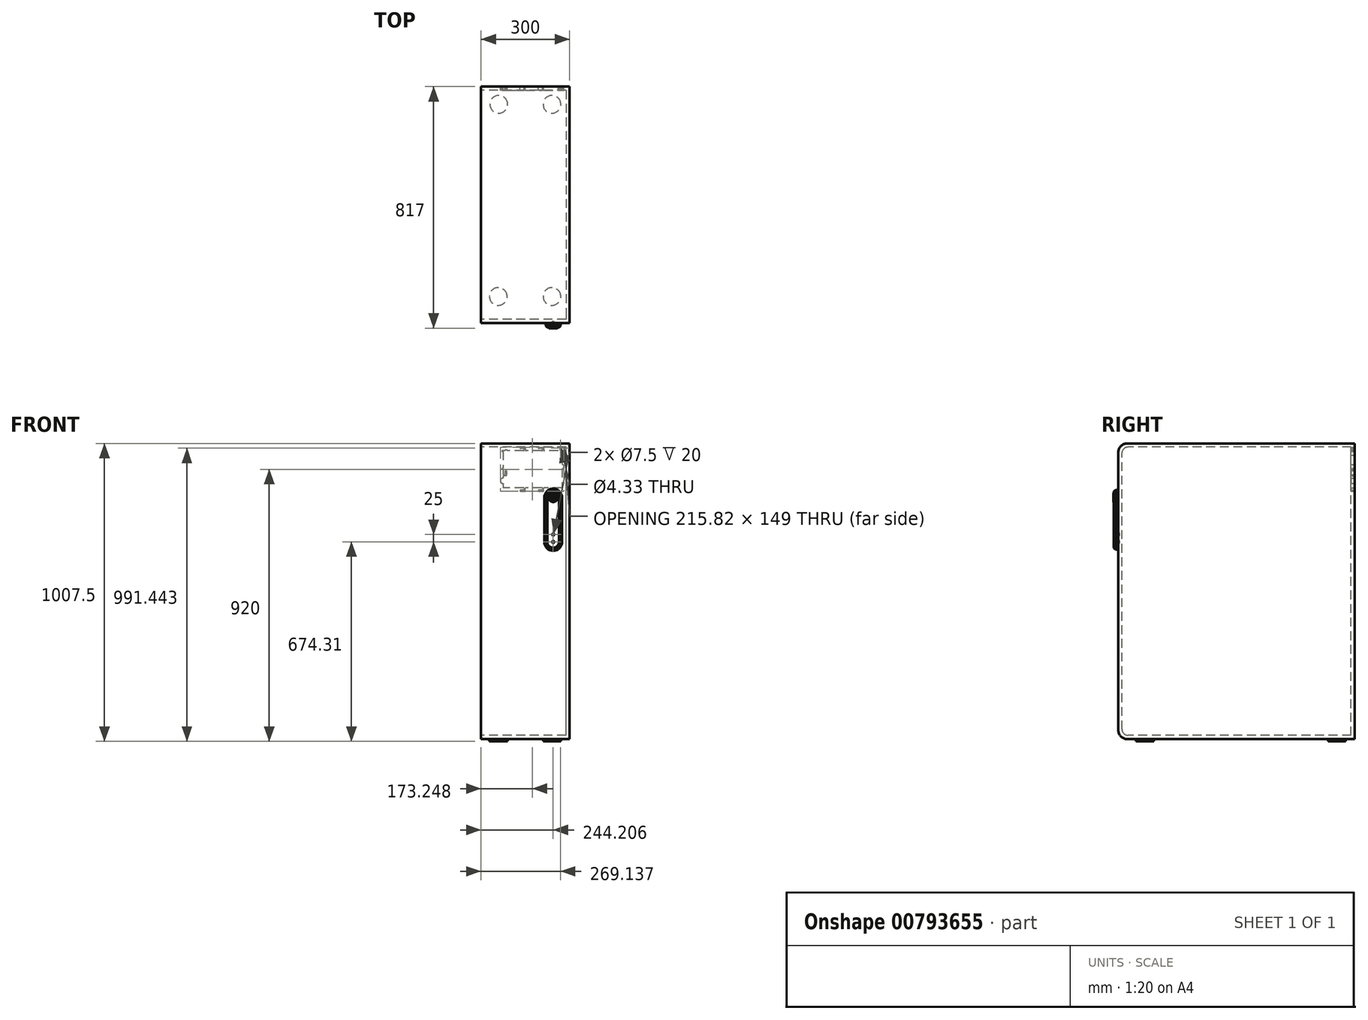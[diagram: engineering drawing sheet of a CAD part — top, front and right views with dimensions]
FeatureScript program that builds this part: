
annotation { "Feature Type Name" : "Feature", "Feature Type Description" : "" }
export const myFeature = defineFeature(function(context is Context, id is Id, definition is map)
    precondition{}
    {
        {
            var Q0;
            Q0=qCreatedBy(makeId("Right.planeOp"),FACE);
            var sketch = newSketch(context, id + "F0", { "sketchPlane" : qUnion([Q0])});
            skLineSegment(sketch, "E0.bottom", {"start": v(400, -500) * mm, "end": v(-400, -500) * mm});
            skLineSegment(sketch, "E0.top", {"start": v(400, 500) * mm, "end": v(-400, 500) * mm});
            skLineSegment(sketch, "E0.left", {"start": v(400, -500) * mm, "end": v(400, 500) * mm});
            skLineSegment(sketch, "E0.right", {"start": v(-400, -500) * mm, "end": v(-400, 500) * mm});
            skPoint(sketch, "E0.middle", {"position": v(0, 0) * mm});
            skSolve(sketch);
        }
        {
            var Q0;
            Q0=makeQuery(id+"F0.imprint","IMPRINT",FACE,{"disambiguationData":[TD([[makeQuery(id+"F0.imprint","IMPRINT",EDGE,{"derivedFrom":sQuery(id+"F0.wireOp",EDGE,"E0.bottom")}),-1.0]])]});
            extrude(context, id + "F1", {"entities" : qUnion([Q0]), "depth" : 300 * mm, "offsetDistance" : 25 * mm});
        }
        {
            var Q0;
            Q0=makeQuery(id+"F1.opExtrude","SWEPT_EDGE",EDGE,{"disambiguationData":[OSD([sQuery(id+"F0.wireOp",EDGE,"E0.top"),sQuery(id+"F0.wireOp",EDGE,"E0.right")])]});
            var Q1;
            Q1=makeQuery(id+"F1.opExtrude","SWEPT_EDGE",EDGE,{"disambiguationData":[OSD([sQuery(id+"F0.wireOp",EDGE,"E0.bottom"),sQuery(id+"F0.wireOp",EDGE,"E0.right")])]});
            fillet(context, id + "F2", {"entities" : qUnion([Q0, Q1]), "radius" : 30 * mm, "tangentPropagation" : true, "allowEdgeOverflow" : false});
        }
        {
            var Q0;
            Q0=makeQuery(id+"F1.opExtrude","CAP_FACE",FACE,{"disambiguationData":[OSD([sQuery(id+"F0.wireOp",EDGE,"E0.bottom"),sQuery(id+"F0.wireOp",EDGE,"E0.top"),sQuery(id+"F0.wireOp",EDGE,"E0.left"),sQuery(id+"F0.wireOp",EDGE,"E0.right")])],"isStart":true});
            var sketch = newSketch(context, id + "F3", { "sketchPlane" : qUnion([Q0])});
            skLineSegment(sketch, "E1.bottom", {"start": v(-387.5, -487.5) * mm, "end": v(367.5, -487.5) * mm});
            skLineSegment(sketch, "E1.top", {"start": v(-387.5, 487.5) * mm, "end": v(367.5, 487.5) * mm});
            skLineSegment(sketch, "E1.left", {"start": v(-387.5, -487.5) * mm, "end": v(-387.5, 487.5) * mm});
            skLineSegment(sketch, "E1.right", {"start": v(387.5, -467.5) * mm, "end": v(387.5, 467.5) * mm});
            skPoint(sketch, "E1.middle", {"position": v(0, 0) * mm});
            skPoint(sketch, "E2.visualSharp", {"position": v(387.5, 487.5) * mm});
            skArc(sketch, "E2.filletArc", {"start": v(387.5, 467.5) * mm, "mid": v(381.64, 481.64) * mm, "end": v(367.5, 487.5) * mm});
            skPoint(sketch, "E3.visualSharp", {"position": v(387.5, -487.5) * mm});
            skArc(sketch, "E3.filletArc", {"start": v(367.5, -487.5) * mm, "mid": v(381.64, -481.64) * mm, "end": v(387.5, -467.5) * mm});
            skSolve(sketch);
        }
        {
            var Q0;
            Q0=makeQuery(id+"F3.imprint","IMPRINT",FACE,{"disambiguationData":[TD([[makeQuery(id+"F3.imprint","IMPRINT",EDGE,{"derivedFrom":sQuery(id+"F3.wireOp",EDGE,"E1.bottom")}),1.0]])]});
            extrude(context, id + "F4", {"entities" : qUnion([Q0]), "operationType" : NewBodyOperationType.REMOVE, "oppositeDirection" : true, "depth" : 287.5 * mm, "offsetDistance" : 25 * mm});
        }
        {
            var Q0;
            Q0=makeQuery(id+"F1.opExtrude","SWEPT_FACE",FACE,{"disambiguationData":[OSD([sQuery(id+"F0.wireOp",EDGE,"E0.left")])]});
            var sketch = newSketch(context, id + "F5", { "sketchPlane" : qUnion([Q0])});
            skLineSegment(sketch, "E4.bottom", {"start": v(-261.46, 475) * mm, "end": v(-214.12, 475) * mm});
            skLineSegment(sketch, "E4.top", {"start": v(-274.34, 350) * mm, "end": v(-214.12, 350) * mm});
            skLineSegment(sketch, "E4.left", {"start": v(-274.34, 459.64) * mm, "end": v(-274.34, 428.5) * mm});
            skLineSegment(sketch, "E4.right", {"start": v(-74.34, 473) * mm, "end": v(-74.34, 415.52) * mm});
            skLineSegment(sketch, "E5", {"start": v(-74.34, 475) * mm, "end": v(-71.34, 475) * mm});
            skLineSegment(sketch, "E6", {"start": v(-70.34, 474) * mm, "end": v(-70.34, 474) * mm});
            skLineSegment(sketch, "E7", {"start": v(-71.34, 473) * mm, "end": v(-74.34, 473) * mm});
            skPoint(sketch, "E8.visualSharp", {"position": v(-70.34, 473) * mm});
            skArc(sketch, "E8.filletArc", {"start": v(-71.34, 473) * mm, "mid": v(-70.63, 473.3) * mm, "end": v(-70.34, 474) * mm});
            skPoint(sketch, "E9.visualSharp", {"position": v(-70.34, 475) * mm});
            skArc(sketch, "E9.filletArc", {"start": v(-70.34, 474) * mm, "mid": v(-70.63, 474.7) * mm, "end": v(-71.34, 475) * mm});
            skArc(sketch, "E10", {"start": v(-81.43, 475) * mm, "mid": v(-84.93, 478.5) * mm, "end": v(-88.43, 475) * mm});
            skLineSegment(sketch, "E11.trimOffspring", {"start": v(-81.43, 475) * mm, "end": v(-74.34, 475) * mm});
            skLineSegment(sketch, "E12", {"start": v(-146.17, 477) * mm, "end": v(-146.17, 481) * mm});
            skLineSegment(sketch, "E13", {"start": v(-144.17, 483) * mm, "end": v(-134.17, 483) * mm});
            skLineSegment(sketch, "E14", {"start": v(-134.17, 487) * mm, "end": v(-148.17, 487) * mm});
            skLineSegment(sketch, "E15", {"start": v(-150.17, 485) * mm, "end": v(-150.17, 477) * mm});
            skArc(sketch, "E16", {"start": v(-134.17, 483) * mm, "mid": v(-132.17, 485) * mm, "end": v(-134.17, 487) * mm});
            skPoint(sketch, "E17.visualSharp", {"position": v(-146.17, 483) * mm});
            skArc(sketch, "E17.filletArc", {"start": v(-144.17, 483) * mm, "mid": v(-145.58, 482.41) * mm, "end": v(-146.17, 481) * mm});
            skArc(sketch, "E18.filletArc", {"start": v(-148.17, 487) * mm, "mid": v(-149.58, 486.41) * mm, "end": v(-150.17, 485) * mm});
            skLineSegment(sketch, "E19.trimOffspring", {"start": v(-144.17, 475) * mm, "end": v(-88.43, 475) * mm});
            skPoint(sketch, "E20.visualSharp", {"position": v(-146.17, 475) * mm});
            skArc(sketch, "E20.filletArc", {"start": v(-146.17, 477) * mm, "mid": v(-145.58, 475.59) * mm, "end": v(-144.17, 475) * mm});
            skPoint(sketch, "E21.visualSharp", {"position": v(-150.17, 475) * mm});
            skArc(sketch, "E21.filletArc", {"start": v(-152.17, 475) * mm, "mid": v(-150.75, 475.59) * mm, "end": v(-150.17, 477) * mm});
            skLineSegment(sketch, "E22", {"start": v(-208.12, 477) * mm, "end": v(-208.12, 481) * mm});
            skLineSegment(sketch, "E23", {"start": v(-206.12, 483) * mm, "end": v(-196.12, 483) * mm});
            skLineSegment(sketch, "E24", {"start": v(-196.12, 487) * mm, "end": v(-210.12, 487) * mm});
            skLineSegment(sketch, "E25", {"start": v(-212.12, 485) * mm, "end": v(-212.12, 477) * mm});
            skArc(sketch, "E26", {"start": v(-196.12, 483) * mm, "mid": v(-194.12, 485) * mm, "end": v(-196.12, 487) * mm});
            skPoint(sketch, "E27.visualSharp", {"position": v(-208.12, 483) * mm});
            skArc(sketch, "E27.filletArc", {"start": v(-206.12, 483) * mm, "mid": v(-207.53, 482.41) * mm, "end": v(-208.12, 481) * mm});
            skPoint(sketch, "E28.visualSharp", {"position": v(-212.12, 487) * mm});
            skArc(sketch, "E28.filletArc", {"start": v(-210.12, 487) * mm, "mid": v(-211.53, 486.41) * mm, "end": v(-212.12, 485) * mm});
            skLineSegment(sketch, "E29.trimOffspring", {"start": v(-206.12, 475) * mm, "end": v(-152.17, 475) * mm});
            skPoint(sketch, "E30.visualSharp", {"position": v(-208.12, 475) * mm});
            skArc(sketch, "E30.filletArc", {"start": v(-208.12, 477) * mm, "mid": v(-207.53, 475.59) * mm, "end": v(-206.12, 475) * mm});
            skPoint(sketch, "E31.visualSharp", {"position": v(-212.12, 475) * mm});
            skArc(sketch, "E31.filletArc", {"start": v(-214.12, 475) * mm, "mid": v(-212.7, 475.59) * mm, "end": v(-212.12, 477) * mm});
            skArc(sketch, "E32", {"start": v(-261.46, 475) * mm, "mid": v(-276.92, 474.87) * mm, "end": v(-274.34, 459.64) * mm});
            skCircle(sketch, "E33", {"center": v(-269.14, 483.94) * mm, "radius": 2.16 * mm});
            skArc(sketch, "E34", {"start": v(-274.34, 428.5) * mm, "mid": v(-281.16, 421.68) * mm, "end": v(-274.34, 414.86) * mm});
            skLineSegment(sketch, "E35.trimOffspring", {"start": v(-274.34, 414.86) * mm, "end": v(-274.34, 350) * mm});
            skLineSegment(sketch, "E36", {"start": v(-208.12, 348) * mm, "end": v(-208.12, 344) * mm});
            skLineSegment(sketch, "E37", {"start": v(-206.12, 342) * mm, "end": v(-196.12, 342) * mm});
            skLineSegment(sketch, "E38", {"start": v(-196.12, 338) * mm, "end": v(-210.12, 338) * mm});
            skLineSegment(sketch, "E39", {"start": v(-212.12, 340) * mm, "end": v(-212.12, 348) * mm});
            skArc(sketch, "E40", {"start": v(-196.12, 338) * mm, "mid": v(-194.12, 340) * mm, "end": v(-196.12, 342) * mm});
            skPoint(sketch, "E41.visualSharp", {"position": v(-212.12, 338) * mm});
            skArc(sketch, "E41.filletArc", {"start": v(-212.12, 340) * mm, "mid": v(-211.53, 338.59) * mm, "end": v(-210.12, 338) * mm});
            skPoint(sketch, "E42.visualSharp", {"position": v(-208.12, 342) * mm});
            skArc(sketch, "E42.filletArc", {"start": v(-208.12, 344) * mm, "mid": v(-207.53, 342.59) * mm, "end": v(-206.12, 342) * mm});
            skPoint(sketch, "E43", {"position": v(-208.12, 350) * mm});
            skPoint(sketch, "E44", {"position": v(-212.12, 350) * mm});
            skLineSegment(sketch, "E45.trimOffspring", {"start": v(-206.12, 350) * mm, "end": v(-152.17, 350) * mm});
            skArc(sketch, "E46.filletArc", {"start": v(-206.12, 350) * mm, "mid": v(-207.53, 349.41) * mm, "end": v(-208.12, 348) * mm});
            skArc(sketch, "E47.filletArc", {"start": v(-212.12, 348) * mm, "mid": v(-212.7, 349.41) * mm, "end": v(-214.12, 350) * mm});
            skLineSegment(sketch, "E48", {"start": v(-146.17, 348) * mm, "end": v(-146.17, 344) * mm});
            skLineSegment(sketch, "E49", {"start": v(-144.17, 342) * mm, "end": v(-134.17, 342) * mm});
            skLineSegment(sketch, "E50", {"start": v(-134.17, 338) * mm, "end": v(-148.17, 338) * mm});
            skLineSegment(sketch, "E51", {"start": v(-150.17, 340) * mm, "end": v(-150.17, 348) * mm});
            skArc(sketch, "E52", {"start": v(-134.17, 338) * mm, "mid": v(-132.17, 340) * mm, "end": v(-134.17, 342) * mm});
            skLineSegment(sketch, "E53.trimOffspring", {"start": v(-144.17, 350) * mm, "end": v(-74.34, 350) * mm});
            skPoint(sketch, "E54.visualSharp", {"position": v(-146.17, 342) * mm});
            skArc(sketch, "E54.filletArc", {"start": v(-146.17, 344) * mm, "mid": v(-145.58, 342.59) * mm, "end": v(-144.17, 342) * mm});
            skPoint(sketch, "E55.visualSharp", {"position": v(-150.17, 338) * mm});
            skArc(sketch, "E55.filletArc", {"start": v(-150.17, 340) * mm, "mid": v(-149.58, 338.59) * mm, "end": v(-148.17, 338) * mm});
            skPoint(sketch, "E56.visualSharp", {"position": v(-150.17, 350) * mm});
            skArc(sketch, "E56.filletArc", {"start": v(-150.17, 348) * mm, "mid": v(-150.75, 349.41) * mm, "end": v(-152.17, 350) * mm});
            skPoint(sketch, "E57.visualSharp", {"position": v(-146.17, 350) * mm});
            skArc(sketch, "E57.filletArc", {"start": v(-144.17, 350) * mm, "mid": v(-145.58, 349.41) * mm, "end": v(-146.17, 348) * mm});
            skArc(sketch, "E58", {"start": v(-74.34, 364.4) * mm, "mid": v(-65.34, 373.4) * mm, "end": v(-74.34, 382.4) * mm});
            skLineSegment(sketch, "E59.trimOffspring", {"start": v(-74.34, 364.4) * mm, "end": v(-74.34, 350) * mm});
            skLineSegment(sketch, "E60", {"start": v(-76.34, 394.44) * mm, "end": v(-80.34, 394.44) * mm});
            skLineSegment(sketch, "E61", {"start": v(-82.34, 396.44) * mm, "end": v(-82.34, 406.44) * mm});
            skLineSegment(sketch, "E62", {"start": v(-86.34, 406.44) * mm, "end": v(-86.34, 392.44) * mm});
            skLineSegment(sketch, "E63", {"start": v(-84.34, 390.44) * mm, "end": v(-76.34, 390.44) * mm});
            skArc(sketch, "E64", {"start": v(-82.34, 406.44) * mm, "mid": v(-84.34, 408.44) * mm, "end": v(-86.34, 406.44) * mm});
            skPoint(sketch, "E65.visualSharp", {"position": v(-86.34, 390.44) * mm});
            skArc(sketch, "E65.filletArc", {"start": v(-86.34, 392.44) * mm, "mid": v(-85.75, 391.03) * mm, "end": v(-84.34, 390.44) * mm});
            skPoint(sketch, "E66.visualSharp", {"position": v(-82.34, 394.44) * mm});
            skArc(sketch, "E66.filletArc", {"start": v(-82.34, 396.44) * mm, "mid": v(-81.75, 395.03) * mm, "end": v(-80.34, 394.44) * mm});
            skPoint(sketch, "E67", {"position": v(-74.34, 390.44) * mm});
            skPoint(sketch, "E68", {"position": v(-74.34, 394.44) * mm});
            skLineSegment(sketch, "E69.trimOffspring", {"start": v(-74.34, 388.44) * mm, "end": v(-74.34, 382.4) * mm});
            skArc(sketch, "E70.filletArc", {"start": v(-74.34, 388.44) * mm, "mid": v(-74.92, 389.86) * mm, "end": v(-76.34, 390.44) * mm});
            skArc(sketch, "E71.filletArc", {"start": v(-76.34, 394.44) * mm, "mid": v(-74.92, 395.03) * mm, "end": v(-74.34, 396.44) * mm});
            skLineSegment(sketch, "E72.bottom", {"start": v(-74.34, 413.52) * mm, "end": v(-71.34, 413.52) * mm});
            skLineSegment(sketch, "E72.top", {"start": v(-74.34, 415.52) * mm, "end": v(-71.34, 415.52) * mm});
            skLineSegment(sketch, "E73.trimOffspring", {"start": v(-74.34, 413.52) * mm, "end": v(-74.34, 396.44) * mm});
            skArc(sketch, "E74", {"start": v(-71.34, 413.52) * mm, "mid": v(-70.34, 414.52) * mm, "end": v(-71.34, 415.52) * mm});
            skSolve(sketch);
        }
        {
            var Q0;
            Q0=makeQuery(id+"F5.imprint","IMPRINT",FACE,{"disambiguationData":[TD([[makeQuery(id+"F5.imprint","IMPRINT",EDGE,{"derivedFrom":sQuery(id+"F5.wireOp",EDGE,"E4.bottom")}),-1.0]])]});
            var Q1;
            Q1=makeQuery(id+"F5.imprint","IMPRINT",FACE,{"disambiguationData":[TD([[makeQuery(id+"F5.imprint","IMPRINT",EDGE,{"derivedFrom":sQuery(id+"F5.wireOp",EDGE,"E33")}),1.0]])]});
            extrude(context, id + "F6", {"entities" : qUnion([Q0, Q1]), "operationType" : NewBodyOperationType.REMOVE, "oppositeDirection" : true, "depth" : 25 * mm, "offsetDistance" : 25 * mm});
        }
        {
            var Q0;
            Q0=makeQuery(id+"F1.opExtrude","SWEPT_FACE",FACE,{"disambiguationData":[OSD([sQuery(id+"F0.wireOp",EDGE,"E0.right")])]});
            var sketch = newSketch(context, id + "F7", { "sketchPlane" : qUnion([Q0])});
            skLineSegment(sketch, "E75.bottom", {"start": v(244.2, 341.8) * mm, "end": v(244.2, 341.8) * mm});
            skLineSegment(sketch, "E75.top", {"start": v(244.2, 141.8) * mm, "end": v(244.2, 141.8) * mm});
            skLineSegment(sketch, "E75.left", {"start": v(219.2, 316.8) * mm, "end": v(219.2, 166.8) * mm});
            skLineSegment(sketch, "E75.right", {"start": v(269.2, 316.8) * mm, "end": v(269.2, 166.8) * mm});
            skPoint(sketch, "E76.visualSharp", {"position": v(219.2, 341.8) * mm});
            skArc(sketch, "E76.filletArc", {"start": v(244.2, 341.8) * mm, "mid": v(226.53, 334.49) * mm, "end": v(219.2, 316.8) * mm});
            skPoint(sketch, "E77.visualSharp", {"position": v(269.2, 341.8) * mm});
            skArc(sketch, "E77.filletArc", {"start": v(269.2, 316.8) * mm, "mid": v(261.88, 334.49) * mm, "end": v(244.2, 341.8) * mm});
            skPoint(sketch, "E78.visualSharp", {"position": v(269.2, 141.8) * mm});
            skArc(sketch, "E78.filletArc", {"start": v(244.2, 141.8) * mm, "mid": v(261.88, 149.13) * mm, "end": v(269.2, 166.8) * mm});
            skPoint(sketch, "E79.visualSharp", {"position": v(219.2, 141.8) * mm});
            skArc(sketch, "E79.filletArc", {"start": v(219.2, 166.8) * mm, "mid": v(226.53, 149.13) * mm, "end": v(244.2, 141.8) * mm});
            skSolve(sketch);
        }
        {
            var Q0;
            Q0=makeQuery(id+"F7.imprint","IMPRINT",FACE,{"disambiguationData":[TD([[makeQuery(id+"F7.imprint","IMPRINT",EDGE,{"derivedFrom":sQuery(id+"F7.wireOp",EDGE,"E75.left")}),1.0]])]});
            extrude(context, id + "F8", {"entities" : qUnion([Q0]), "operationType" : NewBodyOperationType.ADD, "depth" : 15 * mm, "offsetDistance" : 25 * mm});
        }
        {
            var Q0;
            Q0=makeQuery(id+"F8.opExtrude","SWEPT_FACE",FACE,{"disambiguationData":[OSD([sQuery(id+"F7.wireOp",EDGE,"E75.left")])]});
            chamfer(context, id + "F9", {"entities" : qUnion([Q0]), "width" : 5 * mm, "tangentPropagation" : true});
        }
        {
            var Q0;
            Q0=makeQuery(id+"F8.opExtrude","CAP_FACE",FACE,{"disambiguationData":[OSD([sQuery(id+"F7.wireOp",EDGE,"E75.left"),sQuery(id+"F7.wireOp",EDGE,"E75.right"),sQuery(id+"F7.wireOp",EDGE,"E76.filletArc"),sQuery(id+"F7.wireOp",EDGE,"E77.filletArc"),sQuery(id+"F7.wireOp",EDGE,"E78.filletArc"),sQuery(id+"F7.wireOp",EDGE,"E79.filletArc")])],"isStart":false});
            var sketch = newSketch(context, id + "F10", { "sketchPlane" : qUnion([Q0])});
            skCircle(sketch, "E80", {"center": v(244.2, 316.8) * mm, "radius": 15 * mm});
            skArc(sketch, "E81", {"start": v(238.13, 321.9) * mm, "mid": v(244.2, 308.88) * mm, "end": v(250.28, 321.9) * mm});
            skArc(sketch, "E82", {"start": v(236, 323.7) * mm, "mid": v(244.2, 306.1) * mm, "end": v(252.4, 323.7) * mm});
            skArc(sketch, "E83", {"start": v(252.4, 323.7) * mm, "mid": v(250.45, 323.86) * mm, "end": v(250.28, 321.9) * mm});
            skArc(sketch, "E84", {"start": v(238.13, 321.9) * mm, "mid": v(237.96, 323.86) * mm, "end": v(236, 323.7) * mm});
            skArc(sketch, "E85", {"start": v(243.51, 316.8) * mm, "mid": v(244.2, 316.12) * mm, "end": v(244.9, 316.8) * mm});
            skLineSegment(sketch, "E86", {"start": v(244.9, 316.8) * mm, "end": v(244.9, 327.51) * mm});
            skLineSegment(sketch, "E87", {"start": v(243.51, 316.8) * mm, "end": v(243.51, 327.51) * mm});
            skArc(sketch, "E88", {"start": v(244.9, 327.51) * mm, "mid": v(244.2, 328.2) * mm, "end": v(243.51, 327.51) * mm});
            skSolve(sketch);
        }
        {
            var Q0;
            Q0=makeQuery(id+"F10.imprint","IMPRINT",FACE,{"disambiguationData":[TD([[makeQuery(id+"F10.imprint","IMPRINT",EDGE,{"derivedFrom":sQuery(id+"F10.wireOp",EDGE,"E80")}),1.0]])]});
            extrude(context, id + "F11", {"entities" : qUnion([Q0]), "operationType" : NewBodyOperationType.ADD, "depth" : 2 * mm, "offsetDistance" : 25 * mm});
        }
        {
            var Q0;
            {var subQ0=sQuery(id+"F7.wireOp",EDGE,"E79.filletArc");var subQ1=sQuery(id+"F7.wireOp",EDGE,"E78.filletArc");var subQ2=sQuery(id+"F7.wireOp",EDGE,"E77.filletArc");var subQ3=sQuery(id+"F7.wireOp",EDGE,"E76.filletArc");var subQ4=sQuery(id+"F7.wireOp",EDGE,"E75.right");var subQ5=sQuery(id+"F7.wireOp",EDGE,"E75.left");Q0=makeQuery(id+"F11.boolean.opBoolean","SPLIT",FACE,{"disambiguationData":[TD([makeQuery(id+"F11.opExtrude","SWEPT_FACE",FACE,{"disambiguationData":[OSD([sQuery(id+"F10.wireOp",EDGE,"E80")])]})])],"derivedFrom":makeQuery(id+"F8.opExtrude","CAP_FACE",FACE,{"disambiguationData":[OSD([subQ5,subQ4,subQ3,subQ2,subQ1,subQ0])],"isStart":false})});}
            var sketch = newSketch(context, id + "F12", { "sketchPlane" : qUnion([Q0])});
            skCircle(sketch, "E89", {"center": v(244.2, 166.8) * mm, "radius": 3.75 * mm});
            skCircle(sketch, "E90", {"center": v(244.2, 191.8) * mm, "radius": 3.75 * mm});
            skSolve(sketch);
        }
        {
            var Q0;
            Q0=makeQuery(id+"F12.imprint","IMPRINT",FACE,{"disambiguationData":[TD([[makeQuery(id+"F12.imprint","IMPRINT",EDGE,{"derivedFrom":sQuery(id+"F12.wireOp",EDGE,"E90")}),1.0]])]});
            var Q1;
            Q1=makeQuery(id+"F12.imprint","IMPRINT",FACE,{"disambiguationData":[TD([[makeQuery(id+"F12.imprint","IMPRINT",EDGE,{"derivedFrom":sQuery(id+"F12.wireOp",EDGE,"E89")}),1.0]])]});
            extrude(context, id + "F13", {"entities" : qUnion([Q0, Q1]), "operationType" : NewBodyOperationType.REMOVE, "oppositeDirection" : true, "depth" : 20 * mm, "offsetDistance" : 25 * mm});
        }
        {
            var Q0;
            Q0=makeQuery(id+"F1.opExtrude","SWEPT_FACE",FACE,{"disambiguationData":[OSD([sQuery(id+"F0.wireOp",EDGE,"E0.bottom")])]});
            var sketch = newSketch(context, id + "F14", { "sketchPlane" : qUnion([Q0])});
            skCircle(sketch, "E91", {"center": v(58.35, 310) * mm, "radius": 30 * mm});
            skCircle(sketch, "E92", {"center": v(240, 310) * mm, "radius": 30 * mm});
            skCircle(sketch, "E93", {"center": v(240, -340) * mm, "radius": 30 * mm});
            skCircle(sketch, "E94", {"center": v(60, -340) * mm, "radius": 30 * mm});
            skSolve(sketch);
        }
        {
            var Q0;
            Q0=makeQuery(id+"F14.imprint","IMPRINT",FACE,{"disambiguationData":[TD([[makeQuery(id+"F14.imprint","IMPRINT",EDGE,{"derivedFrom":sQuery(id+"F14.wireOp",EDGE,"E93")}),1.0]])]});
            var Q1;
            Q1=makeQuery(id+"F14.imprint","IMPRINT",FACE,{"disambiguationData":[TD([[makeQuery(id+"F14.imprint","IMPRINT",EDGE,{"derivedFrom":sQuery(id+"F14.wireOp",EDGE,"E94")}),1.0]])]});
            var Q2;
            Q2=makeQuery(id+"F14.imprint","IMPRINT",FACE,{"disambiguationData":[TD([[makeQuery(id+"F14.imprint","IMPRINT",EDGE,{"derivedFrom":sQuery(id+"F14.wireOp",EDGE,"E92")}),1.0]])]});
            var Q3;
            Q3=makeQuery(id+"F14.imprint","IMPRINT",FACE,{"disambiguationData":[TD([[makeQuery(id+"F14.imprint","IMPRINT",EDGE,{"derivedFrom":sQuery(id+"F14.wireOp",EDGE,"E91")}),1.0]])]});
            extrude(context, id + "F15", {"entities" : qUnion([Q0, Q1, Q2, Q3]), "operationType" : NewBodyOperationType.ADD, "depth" : 7.5 * mm, "offsetDistance" : 25 * mm});
        }
    });
